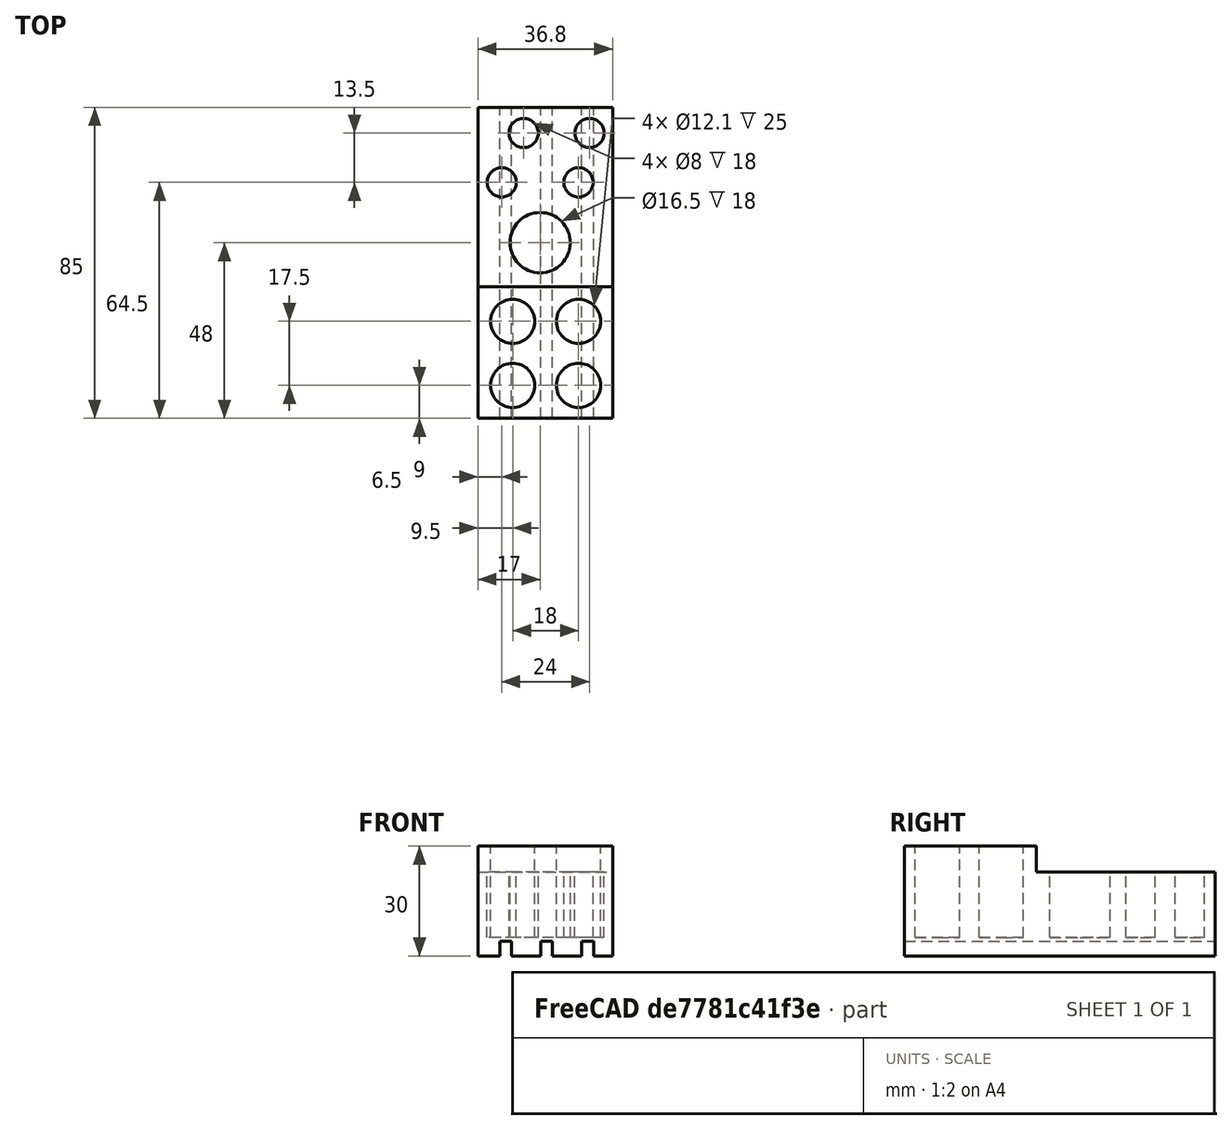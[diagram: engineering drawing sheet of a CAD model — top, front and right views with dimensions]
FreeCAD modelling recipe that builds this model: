
FCSTD DOCUMENT  (FreeCAD 0.18R16093 +53 (Git))
Label: eppendorf_holder_4
License: All rights reserved
LicenseURL: http://en.wikipedia.org/wiki/All_rights_reserved
objects: Part::Cut×13, Part::Cylinder×9, Part::Box×5
note: 27 computed .brp shape members not serialized (recipe doc carries the construction recipe); baked Part::Feature solids carry a one-line shape summary decoded from their .brp

FEATURE [Part::Box] Box  label="Cube"
  AttacherType = Attacher::AttachEngine3D
  Height = 30
  Length = 36.8
  Placement = pos=(0,-3,0) rot=(0,0,1;0rad)
  Width = 85
FEATURE [Part::Cylinder] Cylinder
  Angle = 360
  AttacherType = Attacher::AttachEngine3D
  Height = 25
  Placement = pos=(9.5,6,5) rot=(0,0,1;0rad)
  Radius = 6.05
FEATURE [Part::Cylinder] Cylinder001
  Angle = 360
  AttacherType = Attacher::AttachEngine3D
  Height = 25
  Placement = pos=(27.5,6,5) rot=(0,0,1;0rad)
  Radius = 6.05
FEATURE [Part::Box] Box001  label="Cube001"
  AttacherType = Attacher::AttachEngine3D
  Height = 7
  Length = 40
  Placement = pos=(0,33,23) rot=(0,0,1;0rad)
  Width = 55
FEATURE [Part::Cylinder] Cylinder002
  Angle = 360
  AttacherType = Attacher::AttachEngine3D
  Height = 25
  Placement = pos=(9.5,23.5,5) rot=(0,0,1;0rad)
  Radius = 6.05
FEATURE [Part::Cylinder] Cylinder003
  Angle = 360
  AttacherType = Attacher::AttachEngine3D
  Height = 25
  Placement = pos=(27.5,23.5,5) rot=(0,0,1;0rad)
  Radius = 6.05
FEATURE [Part::Cylinder] Cylinder004
  Angle = 360
  AttacherType = Attacher::AttachEngine3D
  Height = 25
  Placement = pos=(12.5,75,5) rot=(0,0,1;0rad)
  Radius = 4
FEATURE [Part::Cylinder] Cylinder005
  Angle = 360
  AttacherType = Attacher::AttachEngine3D
  Height = 25
  Placement = pos=(27.5,61.5,5) rot=(0,0,1;0rad)
  Radius = 4
FEATURE [Part::Cylinder] Cylinder006
  Angle = 360
  AttacherType = Attacher::AttachEngine3D
  Height = 25
  Placement = pos=(30.5,75,5) rot=(0,0,1;0rad)
  Radius = 4
FEATURE [Part::Cylinder] Cylinder007
  Angle = 360
  AttacherType = Attacher::AttachEngine3D
  Height = 25
  Placement = pos=(6.5,61.5,5) rot=(0,0,1;0rad)
  Radius = 4
FEATURE [Part::Cut] Cut
  Base = -> Box
  Tool = -> Box001
FEATURE [Part::Cut] Cut001
  Base = -> Cut
  Tool = -> Cylinder
FEATURE [Part::Cut] Cut002
  Base = -> Cut001
  Tool = -> Cylinder001
FEATURE [Part::Cut] Cut003
  Base = -> Cut002
  Tool = -> Cylinder002
FEATURE [Part::Cut] Cut004
  Base = -> Cut003
  Tool = -> Cylinder003
FEATURE [Part::Cut] Cut005
  Base = -> Cut004
  Tool = -> Cylinder004
FEATURE [Part::Cut] Cut006
  Base = -> Cut005
  Tool = -> Cylinder005
FEATURE [Part::Cut] Cut007
  Base = -> Cut006
  Tool = -> Cylinder006
FEATURE [Part::Cut] Cut008
  Base = -> Cut007
  Tool = -> Cylinder007
FEATURE [Part::Box] Box004  label="Cube004"
  AttacherType = Attacher::AttachEngine3D
  Height = 4
  Length = 3.2
  Placement = pos=(6,-3,0) rot=(0,0,1;0rad)
  Width = 90
FEATURE [Part::Box] Box006  label="Cube006"
  AttacherType = Attacher::AttachEngine3D
  Height = 4
  Length = 3.2
  Placement = pos=(17.2,-3,0) rot=(0,0,1;0rad)
  Width = 90
FEATURE [Part::Box] Box008  label="Cube008"
  AttacherType = Attacher::AttachEngine3D
  Height = 4
  Length = 3.2
  Placement = pos=(28.4,-3,0) rot=(0,0,1;0rad)
  Width = 90
FEATURE [Part::Cut] Cut009
  Base = -> Cut008
  Tool = -> Box004
FEATURE [Part::Cut] Cut010
  Base = -> Cut009
  Tool = -> Box006
FEATURE [Part::Cut] Cut011
  Base = -> Cut010
  Tool = -> Box008
FEATURE [Part::Cylinder] Cylinder008
  Angle = 360
  AttacherType = Attacher::AttachEngine3D
  Height = 30
  Placement = pos=(17,45,5) rot=(0,0,1;0rad)
  Radius = 8.25
FEATURE [Part::Cut] Cut012
  Base = -> Cut011
  Tool = -> Cylinder008
